# Revit family: 3466A_NX_Network_Interface_Module
name_source: partatom
category: Communication Devices
revit_build: Autodesk Revit 2014 (Build: 20130308_1515(x64)
units: mm (PartAtom-declared; Revit-internal decimal feet)

## types (1)
- 3466A_NX_Network_Interface_Module
    Apparent Load = 0 VA
    Assembly Code = D5090
    Black Material = Paint - Hubbell - Black Matte Textured
    Default Elevation = 48 "
    Description = It provides a simple way to incorporate standard dry contact inputs and outputs into the NX control
    Features = Allows connection of multiple accessory modules in series
• Discovered as a control device and with visibility in the Area
Controller GUI
• Repeats communication signal to extend network length
• Integral link indicators confirm network segment status
• Ribbon cable connection to accessory modules provided
• Power LED indicator confirms presence of accessory DC power
on HubbNET segment
• DIN rail mounting in the NX Accessory Enclosure
    Green Element = Plastic - Hubbell - Green
    Input Power = 24VDC, 800mA max current via HubbNET network cable
    Manufacturer = Hubbell Control Solutions
    Model = NX Dry Contact Module
    Output Power = 24VDC power supplied to connected accessory modules
    Product Page URL = https://www.hubbell.com
    Steel = Metal-Hubbell-Galvanized_Steel
    Type Comments = NX Network Interface Module
    URL = https://www.hubbell.com
    Voltage = 24 V
    Warranty = 5-Years Warranty
    White Element = Glass, White, High Luminance

## geometry (parser evidence)
native form markers: Sweep x1
no freeform markers — native parametric forms only
